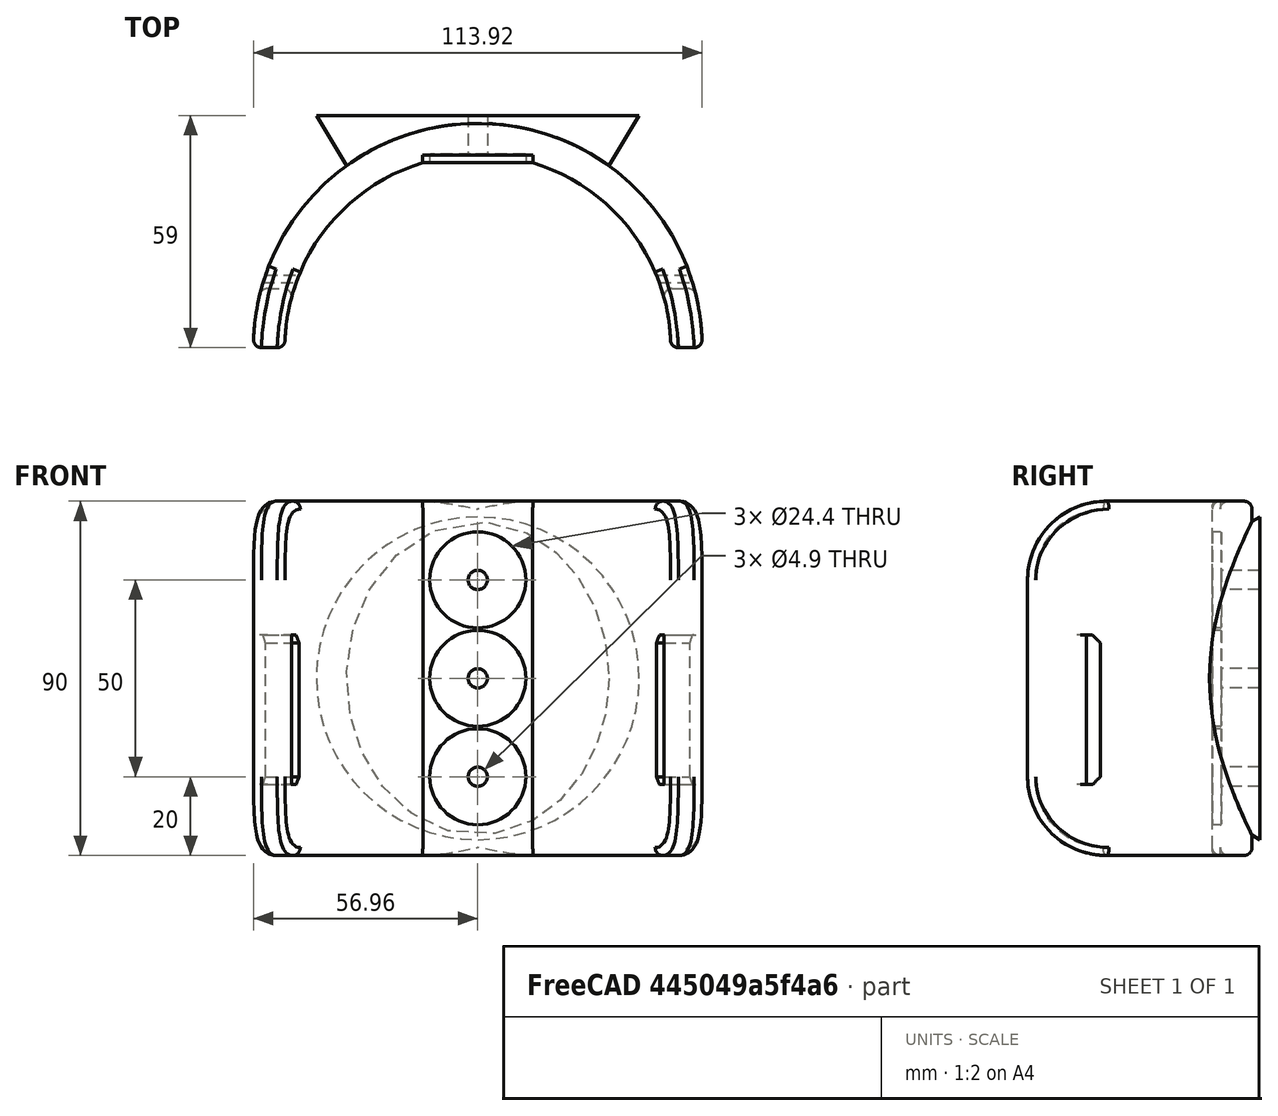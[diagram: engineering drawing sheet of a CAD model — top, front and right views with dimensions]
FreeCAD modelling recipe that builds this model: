
FCSTD DOCUMENT  (FreeCAD 0.19R24276 (Git))
Label: estructuraRozaderaV3
License: All rights reserved
LicenseURL: http://en.wikipedia.org/wiki/All_rights_reserved
objects: TechDraw::DrawViewDimension×13, Part::Cylinder×8, Part::Offset×6, Part::Fillet×5, Part::MultiFuse×4, Part::Cut×4, TechDraw::DrawProjGroupItem×3, Part::Box×2, TechDraw::DrawSVGTemplate×2, TechDraw::DrawViewPart×2, TechDraw::DrawPage×2, Part::Cone×1, Part::Chamfer×1, TechDraw::DrawProjGroup×1, TechDraw::DrawViewAnnotation×1
note: 31 computed .brp shape members not serialized (recipe doc carries the construction recipe); baked Part::Feature solids carry a one-line shape summary decoded from their .brp

FEATURE [Part::Cylinder] Cylinder
  Angle = 180
  AttacherType = Attacher::AttachEngine3D
  Height = 90
  Radius = 49
FEATURE [Part::Cylinder] Cylinder001
  Angle = 180
  AttacherType = Attacher::AttachEngine3D
  Height = 90
  Radius = 57
FEATURE [Part::Box] Box  label="Cube"
  AttacherType = Attacher::AttachEngine3D
  Height = 38
  Length = 200
  Placement = pos=(-101,15,18) rot=(0,0,1;0rad)
  Width = 3.5
FEATURE [Part::Cylinder] Cylinder003
  Angle = 360
  AttacherType = Attacher::AttachEngine3D
  Height = 20
  Placement = pos=(0,60,20) rot=(1,0,0;1.5708rad)
  Radius = 2.25
FEATURE [Part::Cylinder] Cylinder004
  Angle = 360
  AttacherType = Attacher::AttachEngine3D
  Height = 20
  Placement = pos=(0,60,45) rot=(1,0,0;1.5708rad)
  Radius = 2.25
FEATURE [Part::Cylinder] Cylinder005
  Angle = 360
  AttacherType = Attacher::AttachEngine3D
  Height = 20
  Placement = pos=(0,60,70) rot=(1,0,0;1.5708rad)
  Radius = 2.25
FEATURE [Part::Box] Box001  label="Cube001"
  AttacherType = Attacher::AttachEngine3D
  Height = 90
  Length = 28
  Placement = pos=(-14,47,0) rot=(0,0,1;0rad)
  Width = 2
FEATURE [Part::Cone] Cone
  Angle = 360
  AttacherType = Attacher::AttachEngine3D
  Height = 35
  Placement = pos=(0,59,45) rot=(1,0,0;1.5708rad)
  Radius1 = 41
  Radius2 = 20
FEATURE [Part::MultiFuse] Fusion
  Shapes = -> [Cylinder001,Cone]
FEATURE [Part::Cut] Cut
  Base = -> Fusion
  Tool = -> Cylinder
FEATURE [Part::Cut] Cut001
  Base = -> Cut
  Tool = -> Box
FEATURE [Part::Fillet] Fillet
  Base = -> Box001
  Edges = 2 edges r=1: [Edge9,Edge10]
FEATURE [Part::Fillet] Fillet001
  Base = -> Cut001
  Edges = 4 edges r=20: [Edge2,Edge4,Edge18,Edge29]
FEATURE [Part::Fillet] Fillet002
  Base = -> Fillet001
  Edges = 1 edges r=2: [Edge4]
FEATURE [Part::Fillet] Fillet003
  Base = -> Fillet002
  Edges = 1 edges r=2: [Edge3]
FEATURE [Part::MultiFuse] Fusion001
  Shapes = -> [Fillet,Fillet003]
FEATURE [Part::Cylinder] Cylinder006
  Angle = 360
  AttacherType = Attacher::AttachEngine3D
  Height = 2
  Placement = pos=(0,49,45) rot=(1,0,0;1.5708rad)
  Radius = 12
FEATURE [Part::Cylinder] Cylinder007
  Angle = 360
  AttacherType = Attacher::AttachEngine3D
  Height = 2
  Placement = pos=(0,49,20) rot=(1,0,0;1.5708rad)
  Radius = 12
FEATURE [Part::Cylinder] Cylinder008
  Angle = 360
  AttacherType = Attacher::AttachEngine3D
  Height = 2
  Placement = pos=(0,49,70) rot=(1,0,0;1.5708rad)
  Radius = 12
FEATURE [Part::Offset] Offset
  Fill = false
  Intersection = false
  Join = 0
  Mode = 0
  SelfIntersection = false
  Source = -> Cylinder004
  Value = 0.2
FEATURE [Part::Offset] Offset001
  Fill = false
  Intersection = false
  Join = 0
  Mode = 0
  SelfIntersection = false
  Source = -> Cylinder005
  Value = 0.2
FEATURE [Part::Offset] Offset002
  Fill = false
  Intersection = false
  Join = 0
  Mode = 0
  SelfIntersection = false
  Source = -> Cylinder003
  Value = 0.2
FEATURE [Part::MultiFuse] Fusion002
  Shapes = -> [Offset,Offset001,Offset002]
FEATURE [Part::Offset] Offset003
  Fill = false
  Intersection = false
  Join = 0
  Mode = 0
  SelfIntersection = false
  Source = -> Cylinder006
  Value = 0.2
FEATURE [Part::Offset] Offset004
  Fill = false
  Intersection = false
  Join = 0
  Mode = 0
  SelfIntersection = false
  Source = -> Cylinder007
  Value = 0.2
FEATURE [Part::Offset] Offset005
  Fill = false
  Intersection = false
  Join = 0
  Mode = 0
  SelfIntersection = false
  Source = -> Cylinder008
  Value = 0.2
FEATURE [Part::MultiFuse] Fusion003
  Shapes = -> [Offset003,Offset004,Offset005]
FEATURE [Part::Cut] Cut002
  Base = -> Fusion001
  Tool = -> Fusion003
FEATURE [Part::Cut] Cut003
  Base = -> Cut002
  Tool = -> Fusion002
FEATURE [Part::Fillet] Fillet004
  Base = -> Cut003
  Edges = 4 edges r=2: [Edge37,Edge55,Edge80,Edge101]
FEATURE [Part::Chamfer] Chamfer
  Base = -> Fillet004
  Edges = 4 edges r=2: [Edge18,Edge22,Edge141,Edge144]
FEATURE [TechDraw::DrawSVGTemplate] Template
  EditableTexts = Designed_by_Name=<owner>; Drawing_number=001; FC-Date=-; FC-SC=1:3; FC-SH=1/2; FC-Title=Slider Holder; Subtitle=Soporte Deslizadera; Weight=<350gr
  Height = 210
  Orientation = 1
  Width = 297
FEATURE [TechDraw::DrawViewPart] View
  CoarseView = false
  Direction = (0.577,-0.577,0.577)
  Focus = 100
  HardHidden = false
  IsoCount = 0
  IsoHidden = false
  IsoVisible = false
  LockPosition = false
  Perspective = false
  Rotation = 0
  ScaleType = 0
  SeamHidden = false
  SeamVisible = true
  SmoothHidden = false
  SmoothVisible = true
  Source = -> [Chamfer]
  X = 213.955
  XDirection = (0.707,0.707,0)
  Y = 127.597
FEATURE [TechDraw::DrawProjGroupItem] ProjItem  label="Front"
  CoarseView = false
  Direction = (0,-1,0)
  Focus = 100
  HardHidden = false
  IsoCount = 0
  IsoHidden = false
  IsoVisible = false
  LockPosition = true
  Perspective = false
  Rotation = 0
  RotationVector = (1,0,0)
  Scale = 0.5
  ScaleType = 2
  SeamHidden = false
  SeamVisible = true
  SmoothHidden = false
  SmoothVisible = true
  Source = -> [Chamfer]
  Type = 0
  X = 0
  XDirection = (1,0,0)
  Y = 0
FEATURE [TechDraw::DrawProjGroupItem] ProjItem001  label="Top"
  CoarseView = false
  Direction = (0,0,1)
  Focus = 100
  HardHidden = false
  IsoCount = 0
  IsoHidden = false
  IsoVisible = false
  LockPosition = false
  Perspective = false
  Rotation = 0
  RotationVector = (1,0,0)
  ScaleType = 2
  SeamHidden = false
  SeamVisible = true
  SmoothHidden = false
  SmoothVisible = true
  Source = -> [Chamfer]
  Type = 4
  X = 0
  XDirection = (1,0,0)
  Y = -67.75
FEATURE [TechDraw::DrawProjGroupItem] ProjItem002  label="Right"
  CoarseView = false
  Direction = (1,-1e-16,0)
  Focus = 100
  HardHidden = false
  IsoCount = 0
  IsoHidden = false
  IsoVisible = false
  LockPosition = false
  Perspective = false
  Rotation = 0
  RotationVector = (1,0,0)
  ScaleType = 2
  SeamHidden = false
  SeamVisible = true
  SmoothHidden = false
  SmoothVisible = true
  Source = -> [Chamfer]
  Type = 2
  X = -59.2689
  XDirection = (1e-16,1,0)
  Y = 0
FEATURE [TechDraw::DrawProjGroup] ProjGroup
  Anchor = -> ProjItem
  AutoDistribute = true
  LockPosition = false
  ProjectionType = 0
  Rotation = 0
  Scale = 0.5
  ScaleType = 2
  Source = -> [Chamfer]
  Views = -> [ProjItem,ProjItem001,ProjItem002]
  X = 99.0195
  Y = 156.429
  spacingX = 16
  spacingY = 15
FEATURE [TechDraw::DrawViewDimension] Dimension
  Arbitrary = false
  ArbitraryTolerances = false
  EqualTolerance = true
  FormatSpec = %.2f
  FormatSpecOverTolerance = %+.2f
  FormatSpecUnderTolerance = %+.2f
  Inverted = false
  LockPosition = false
  MeasureType = 1
  OverTolerance = 0
  References2D = -> [ProjItem001]
  Rotation = 0
  ScaleType = 0
  TheoreticalExact = false
  Type = 1
  UnderTolerance = 0
  X = 1.8e-15
  Y = -14.75
FEATURE [TechDraw::DrawViewDimension] Dimension001
  Arbitrary = false
  ArbitraryTolerances = false
  EqualTolerance = true
  FormatSpec = %.2f
  FormatSpecOverTolerance = %+.2f
  FormatSpecUnderTolerance = %+.2f
  Inverted = false
  LockPosition = false
  MeasureType = 1
  OverTolerance = 0
  References2D = -> [ProjItem001]
  Rotation = 0
  ScaleType = 0
  TheoreticalExact = false
  Type = 2
  UnderTolerance = 0
  X = -47.6599
  Y = 0.672607
FEATURE [TechDraw::DrawViewDimension] Dimension002
  Arbitrary = false
  ArbitraryTolerances = false
  EqualTolerance = true
  FormatSpec = %.2f
  FormatSpecOverTolerance = %+.2f
  FormatSpecUnderTolerance = %+.2f
  Inverted = false
  LockPosition = false
  MeasureType = 1
  OverTolerance = 0
  References2D = -> [ProjItem]
  Rotation = 0
  ScaleType = 0
  TheoreticalExact = false
  Type = 2
  UnderTolerance = 0
  X = 35.97
  Y = 0.990469
FEATURE [TechDraw::DrawSVGTemplate] Template001
  EditableTexts = Designed_by_Name=<owner>; Drawing_number=001; FC-Date=-; FC-SC=1:3; FC-SH=2/2; FC-Title=Slider Holder; Subtitle=Soporte Deslizadera; Weight=<350
  Height = 210
  Orientation = 1
  Width = 297
FEATURE [TechDraw::DrawViewPart] View001
  CoarseView = false
  Direction = (0.577,-0.577,0.577)
  Focus = 100
  HardHidden = false
  IsoCount = 0
  IsoHidden = false
  IsoVisible = false
  LockPosition = false
  Perspective = false
  Rotation = 0
  ScaleType = 0
  SeamHidden = false
  SeamVisible = true
  SmoothHidden = false
  SmoothVisible = true
  Source = -> [Chamfer]
  X = 155.176
  XDirection = (0.707,0.707,0)
  Y = 125.356
FEATURE [TechDraw::DrawViewDimension] Dimension003
  Arbitrary = false
  ArbitraryTolerances = false
  EqualTolerance = true
  FormatSpec = ⌀%.2f
  FormatSpecOverTolerance = %+.2f
  FormatSpecUnderTolerance = %+.2f
  Inverted = false
  LockPosition = false
  MeasureType = 1
  OverTolerance = 0
  References2D = -> [View001]
  Rotation = 0
  ScaleType = 0
  TheoreticalExact = false
  Type = 5
  UnderTolerance = 0
  X = -10.9091
  Y = 23.3766
FEATURE [TechDraw::DrawViewDimension] Dimension004
  Arbitrary = false
  ArbitraryTolerances = false
  EqualTolerance = true
  FormatSpec = ⌀%.2f
  FormatSpecOverTolerance = %+.2f
  FormatSpecUnderTolerance = %+.2f
  Inverted = false
  LockPosition = false
  MeasureType = 1
  OverTolerance = 0
  References2D = -> [View001]
  Rotation = 0
  ScaleType = 0
  TheoreticalExact = false
  Type = 5
  UnderTolerance = 0
  X = -7.4026
  Y = 4.28571
FEATURE [TechDraw::DrawViewDimension] Dimension005
  Arbitrary = false
  ArbitraryTolerances = false
  EqualTolerance = true
  FormatSpec = %.2f
  FormatSpecOverTolerance = %+.2f
  FormatSpecUnderTolerance = %+.2f
  Inverted = false
  LockPosition = false
  MeasureType = 1
  OverTolerance = 0
  References2D = -> [View001]
  Rotation = 0
  ScaleType = 0
  TheoreticalExact = false
  Type = 2
  UnderTolerance = 0
  X = -97.5437
  Y = 12.5906
FEATURE [TechDraw::DrawViewDimension] Dimension006
  Arbitrary = false
  ArbitraryTolerances = false
  EqualTolerance = true
  FormatSpec = %.2f
  FormatSpecOverTolerance = %+.2f
  FormatSpecUnderTolerance = %+.2f
  Inverted = false
  LockPosition = false
  MeasureType = 1
  OverTolerance = 0
  References2D = -> [View001]
  Rotation = 0
  ScaleType = 0
  TheoreticalExact = false
  Type = 1
  UnderTolerance = 0
  X = -25.5652
  Y = 42.3841
FEATURE [TechDraw::DrawViewDimension] Dimension007
  Arbitrary = false
  ArbitraryTolerances = false
  EqualTolerance = true
  FormatSpec = %.2f
  FormatSpecOverTolerance = %+.2f
  FormatSpecUnderTolerance = %+.2f
  Inverted = false
  LockPosition = false
  MeasureType = 1
  OverTolerance = 0
  References2D = -> [ProjItem001]
  Rotation = 0
  ScaleType = 0
  TheoreticalExact = false
  Type = 1
  UnderTolerance = 0
  X = -0.476445
  Y = 29.6389
FEATURE [TechDraw::DrawViewDimension] Dimension008
  Arbitrary = false
  ArbitraryTolerances = false
  EqualTolerance = true
  FormatSpec = %.2f
  FormatSpecOverTolerance = %+.2f
  FormatSpecUnderTolerance = %+.2f
  Inverted = false
  LockPosition = false
  MeasureType = 1
  OverTolerance = 0
  References2D = -> [View001]
  Rotation = 0
  ScaleType = 0
  TheoreticalExact = false
  Type = 0
  UnderTolerance = 0
  X = -46.6154
  Y = -28.9201
FEATURE [TechDraw::DrawViewDimension] Dimension009
  Arbitrary = false
  ArbitraryTolerances = false
  EqualTolerance = true
  FormatSpec = %.2f
  FormatSpecOverTolerance = %+.2f
  FormatSpecUnderTolerance = %+.2f
  Inverted = false
  LockPosition = false
  MeasureType = 1
  OverTolerance = 0
  References2D = -> [View001]
  Rotation = 0
  ScaleType = 0
  TheoreticalExact = false
  Type = 0
  UnderTolerance = 0
  X = -67.5318
  Y = 47.5167
FEATURE [TechDraw::DrawViewDimension] Dimension010
  Arbitrary = false
  ArbitraryTolerances = false
  EqualTolerance = true
  FormatSpec = %.2f
  FormatSpecOverTolerance = %+.2f
  FormatSpecUnderTolerance = %+.2f
  Inverted = false
  LockPosition = false
  MeasureType = 1
  OverTolerance = 0
  References2D = -> [View001]
  Rotation = 0
  ScaleType = 0
  TheoreticalExact = false
  Type = 0
  UnderTolerance = 0
  X = -29.114
  Y = 61.7643
FEATURE [TechDraw::DrawViewDimension] Dimension011
  Arbitrary = false
  ArbitraryTolerances = false
  EqualTolerance = true
  FormatSpec = %.2f
  FormatSpecOverTolerance = %+.2f
  FormatSpecUnderTolerance = %+.2f
  Inverted = false
  LockPosition = false
  MeasureType = 1
  OverTolerance = 0
  References2D = -> [View001]
  Rotation = 0
  ScaleType = 0
  TheoreticalExact = false
  Type = 0
  UnderTolerance = 0
  X = 65.6625
  Y = -17.7744
FEATURE [TechDraw::DrawViewAnnotation] Annotation
  Font = osifont
  LineSpace = 80
  LockPosition = false
  MaxWidth = -1
  Rotation = 0
  ScaleType = 0
  Text = Aproximate measurements: | Check with 3D piece
  TextSize = 5
  TextStyle = 0
  X = 64.8117
  Y = 71.3377
FEATURE [TechDraw::DrawPage] Page001  label="Cotas"
  KeepUpdated = true
  NextBalloonIndex = 1
  ProjectionType = 0
  Template = -> Template001
  Views = -> [View001,Dimension003,Dimension004,Dimension005,Dimension006,Dimension008,Dimension009,Dimension010,Dimension011,Annotation]
FEATURE [TechDraw::DrawViewDimension] Dimension012
  Arbitrary = false
  ArbitraryTolerances = false
  EqualTolerance = true
  FormatSpec = %.2f
  FormatSpecOverTolerance = %+.2f
  FormatSpecUnderTolerance = %+.2f
  Inverted = false
  LockPosition = false
  MeasureType = 1
  OverTolerance = 0
  References2D = -> [ProjItem001]
  Rotation = 0
  ScaleType = 0
  TheoreticalExact = false
  Type = 6
  UnderTolerance = 0
  X = 43.2185
  Y = 18.2043
FEATURE [TechDraw::DrawPage] Page  label="Vistas"
  KeepUpdated = true
  NextBalloonIndex = 1
  ProjectionType = 0
  Template = -> Template
  Views = -> [View,ProjGroup,Dimension,Dimension001,Dimension002,Dimension007,Dimension012]
